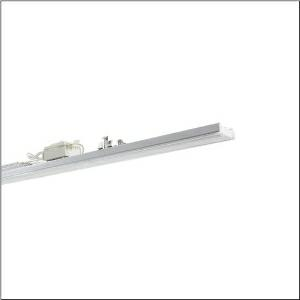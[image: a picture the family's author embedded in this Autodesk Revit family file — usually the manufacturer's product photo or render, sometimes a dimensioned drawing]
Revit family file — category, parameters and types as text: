
# Revit family: licross_r__21_recessed_ho_52te12dv4lxm_5120
name_source: partatom
category: Lighting Fixtures
units: mm (PartAtom-declared; Revit-internal decimal feet)

## family parameters
Cut with Voids When Loaded = No
Host = Face
Light Source = No
Part Type = Normal
Room Calculation Point = No
Round Connector Dimension = Use Diameter
Shared = No

## types (1)
- --- (1 x LED, 20000 lm, 109.8 W, 4000K)
    Apparent Load = 110 VA
    CIE Flux Codes = 69 91 98 100 100
    Color Rendering = 80
    Color Temperature = 4000K
    Default Elevation = 1800 mm
    Description = Licross® 21 Recessed HO, luminaire insert, of sheet steel, galvanised, coil coated, white, length: 2.250mm, width: 66mm, height: 67mm, LED rated luminous flux: 20.000lm, light colour: 840, control gear: DALI 2, with plug, 5-pole, with phase selection, mains connection: 220..240V, AC, 50/60Hz, rated input power: 110W, internal wiring halogen-free, primary optical cover: cover, of PMMA, light emission: direct distribution, primary light characteristic: symmetric, protection rating (complete): IP54, insulation class (complete): insulation class I (protective earthing), certification: CE, ENEC, VDE, UKCA, protection symbol: D if used in an environment with non-conductive dust loads with corresponding accessories, impact resistance: IK06, permissible ambient temperature for indoor applications: -40..+35°C, corresponds to IFS (International Featured Standards) requirements for safety and quality in the food industry, reducing of maximum allowable ambient temperature of 5°C with ceiling mounting, LABS conformity tested according to VDMA 24364:2018-05, packaging unit: 1 piece
    Height = 58 mm
    Lamp = 1 x LED
    Lamp Light Flux = 20000 lm
    Lamp Power = 109.8 W
    Lamp count = 1
    Length = 2250 mm
    Luminous efficacy = 182 lm/W
    Manufacturer = Siteco
    ModVariant = No
    Model = 52TE12DV4LXM
    Mounting Place = Ceiling
    Mounting Type = Pendant
    Number of Poles = 1
    OnlyDefault = Yes
    Power Factor = 1
    Product Name = Licross® 21 Recessed HO
    Product group = luminaire insert | ceiling pendant
    ProductGroupID = 902
    Protection Class = Protection class I
    Protection Degree = IP 54
    RLX_Detail_Level = 1
    RLX_Emergency_Light_Flux = 0 lm
    RLX_Emergency_Type = 0
    RLX_Emergency_Type_DB = No
    RlxData = <blob elided: 29529 chars, md5=b84da489>
    Socket = socket
    Standby Power = 0 W
    System Light Flux = 20000 lm
    System Power = 110 W
    Type Comments = factory setting: luminous flux: 100 % | dim-lin: 254 | 425 mA
    Type Image = l_1296930.jpg
    URL = http://relux.com
    VarID = @adj_138121
    Voltage = 0 V
    Weight = 0.00 kg
    Width = 66 mm

## geometry (parser evidence)
native form markers: Blend x4, Sweep x8
no freeform markers — native parametric forms only
